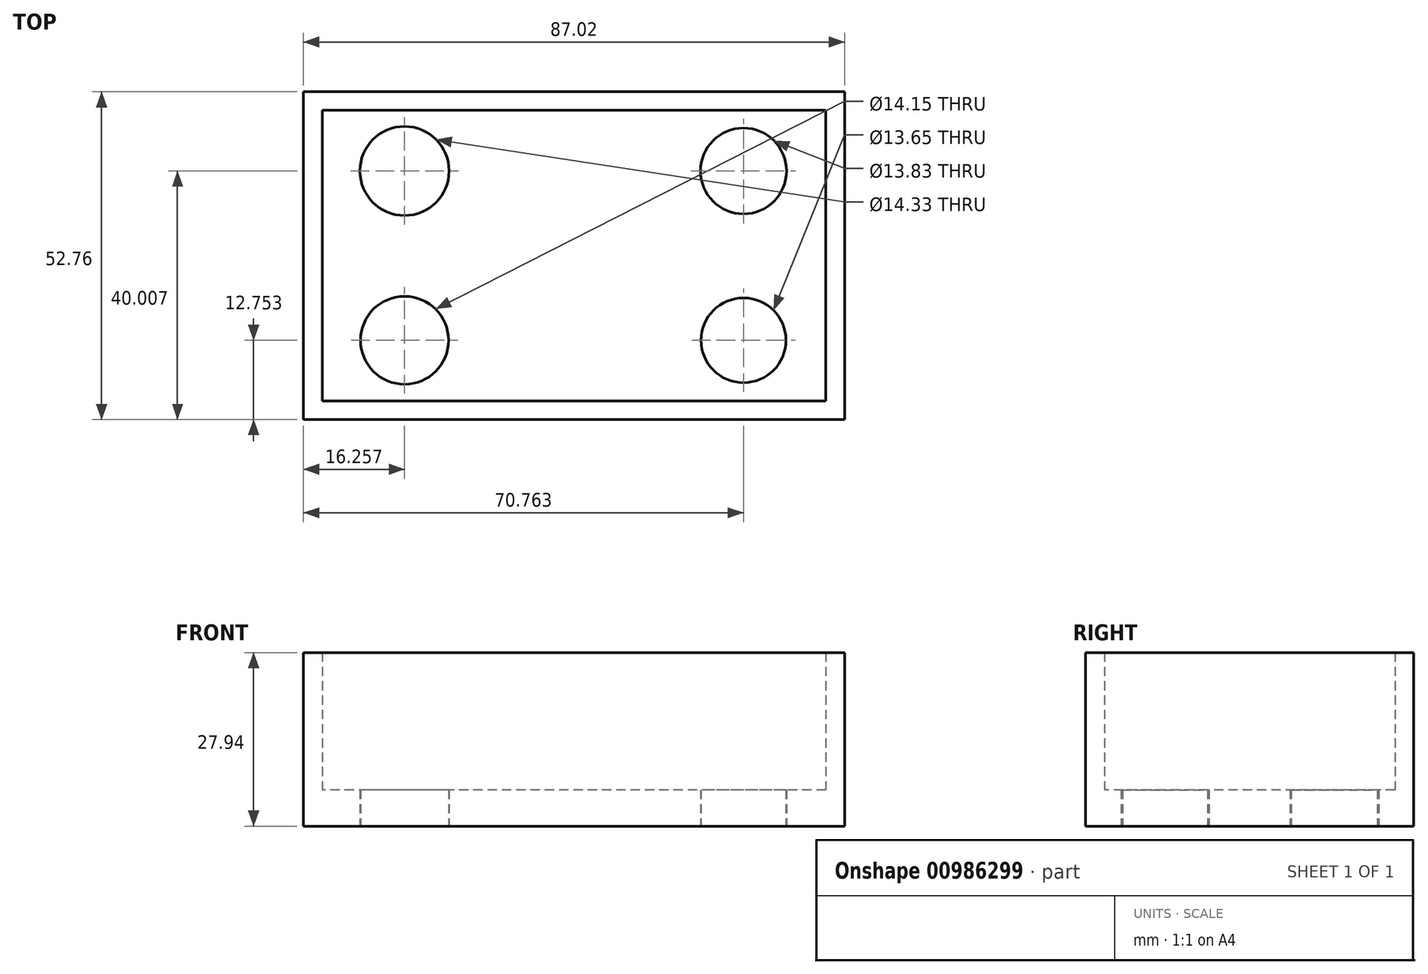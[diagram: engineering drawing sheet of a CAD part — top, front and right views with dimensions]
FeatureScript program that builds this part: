
annotation { "Feature Type Name" : "Feature", "Feature Type Description" : "" }
export const myFeature = defineFeature(function(context is Context, id is Id, definition is map)
    precondition{}
    {
        {
            var Q0;
            Q0=qCreatedBy(makeId("Top.planeOp"),FACE);
            var sketch = newSketch(context, id + "F0", { "sketchPlane" : qUnion([Q0])});
            skLineSegment(sketch, "E0.bottom", {"start": v(40.5, 23.38) * mm, "end": v(-40.5, 23.38) * mm});
            skLineSegment(sketch, "E0.top", {"start": v(40.5, -23.38) * mm, "end": v(-40.5, -23.38) * mm});
            skLineSegment(sketch, "E0.left", {"start": v(40.5, 23.38) * mm, "end": v(40.5, -23.38) * mm});
            skLineSegment(sketch, "E0.right", {"start": v(-40.5, 23.38) * mm, "end": v(-40.5, -23.38) * mm});
            skPoint(sketch, "E0.middle", {"position": v(0, 0) * mm});
            skLineSegment(sketch, "E1.0", {"start": v(43.5, 26.38) * mm, "end": v(-43.5, 26.38) * mm});
            skLineSegment(sketch, "E1.1", {"start": v(43.5, 26.38) * mm, "end": v(43.5, -26.38) * mm});
            skLineSegment(sketch, "E1.2", {"start": v(43.5, -26.38) * mm, "end": v(-43.5, -26.38) * mm});
            skLineSegment(sketch, "E1.3", {"start": v(-43.5, 26.38) * mm, "end": v(-43.5, -26.38) * mm});
            skLineSegment(sketch, "E2.bottom", {"start": v(-27.25, 13.63) * mm, "end": v(27.25, 13.63) * mm, "construction": true});
            skLineSegment(sketch, "E2.top", {"start": v(-27.25, -13.63) * mm, "end": v(27.25, -13.63) * mm, "construction": true});
            skLineSegment(sketch, "E2.left", {"start": v(-27.25, 13.63) * mm, "end": v(-27.25, -13.63) * mm, "construction": true});
            skLineSegment(sketch, "E2.right", {"start": v(27.25, 13.63) * mm, "end": v(27.25, -13.63) * mm, "construction": true});
            skCircle(sketch, "E3", {"center": v(-27.25, 13.63) * mm, "radius": 7.16 * mm});
            skCircle(sketch, "E4", {"center": v(-27.25, -13.63) * mm, "radius": 7.08 * mm});
            skCircle(sketch, "E5", {"center": v(27.25, -13.63) * mm, "radius": 6.82 * mm});
            skCircle(sketch, "E6", {"center": v(27.25, 13.63) * mm, "radius": 6.92 * mm});
            skCircle(sketch, "E7", {"center": v(-27.25, 13.63) * mm, "radius": 4.34 * mm});
            skCircle(sketch, "E8", {"center": v(-27.25, -13.63) * mm, "radius": 3.69 * mm});
            skCircle(sketch, "E9", {"center": v(27.25, -13.63) * mm, "radius": 3.56 * mm});
            skCircle(sketch, "E10", {"center": v(27.25, 13.63) * mm, "radius": 4.16 * mm});
            skSolve(sketch);
        }
        {
            var Q0;
            Q0=makeQuery(id+"F0.imprint","IMPRINT",FACE,{"disambiguationData":[TD([[makeQuery(id+"F0.imprint","IMPRINT",EDGE,{"derivedFrom":sQuery(id+"F0.wireOp",EDGE,"E0.bottom")}),-1.0]])]});
            extrude(context, id + "F1", {"entities" : qUnion([Q0]), "depth" : 27.94 * mm, "offsetDistance" : 25.4 * mm});
        }
        {
            var Q0;
            Q0 = qSketchRegion(id + "F0", true);
            var Q1;
            Q1=makeQuery(id+"F0.imprint","IMPRINT",FACE,{"disambiguationData":[TD([[makeQuery(id+"F0.imprint","IMPRINT",EDGE,{"derivedFrom":sQuery(id+"F0.wireOp",EDGE,"E0.bottom")}),1.0]])]});
            extrude(context, id + "F2", {"entities" : qUnion([Q0, Q1]), "operationType" : NewBodyOperationType.ADD, "depth" : 5.84 * mm, "offsetDistance" : 25.4 * mm});
        }
    });
